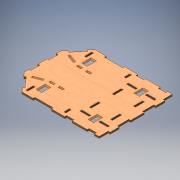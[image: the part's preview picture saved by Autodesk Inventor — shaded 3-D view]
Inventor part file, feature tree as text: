
AUTODESK INVENTOR PART (.ipt)
format: ipt  version: 2019 (Build 230136000, 136)  size: 338,944 bytes
history: native  units: mm
features: extrude x2, sketch x2, other x1
ambient origin geometry x8: Origin, YZ Plane, XZ Plane, XY Plane, X Axis, Y Axis, Z Axis, Center Point
bodies: Body1 (feature_tree)
feature tree (5):
  other  "Твердое тело1"
  extrude  "Выдавливание1"  Depth=25.0mm
  extrude  "Выдавливание2"  Depth=20.0mm
  sketch  "Эскиз1"
  sketch  "Эскиз2"
